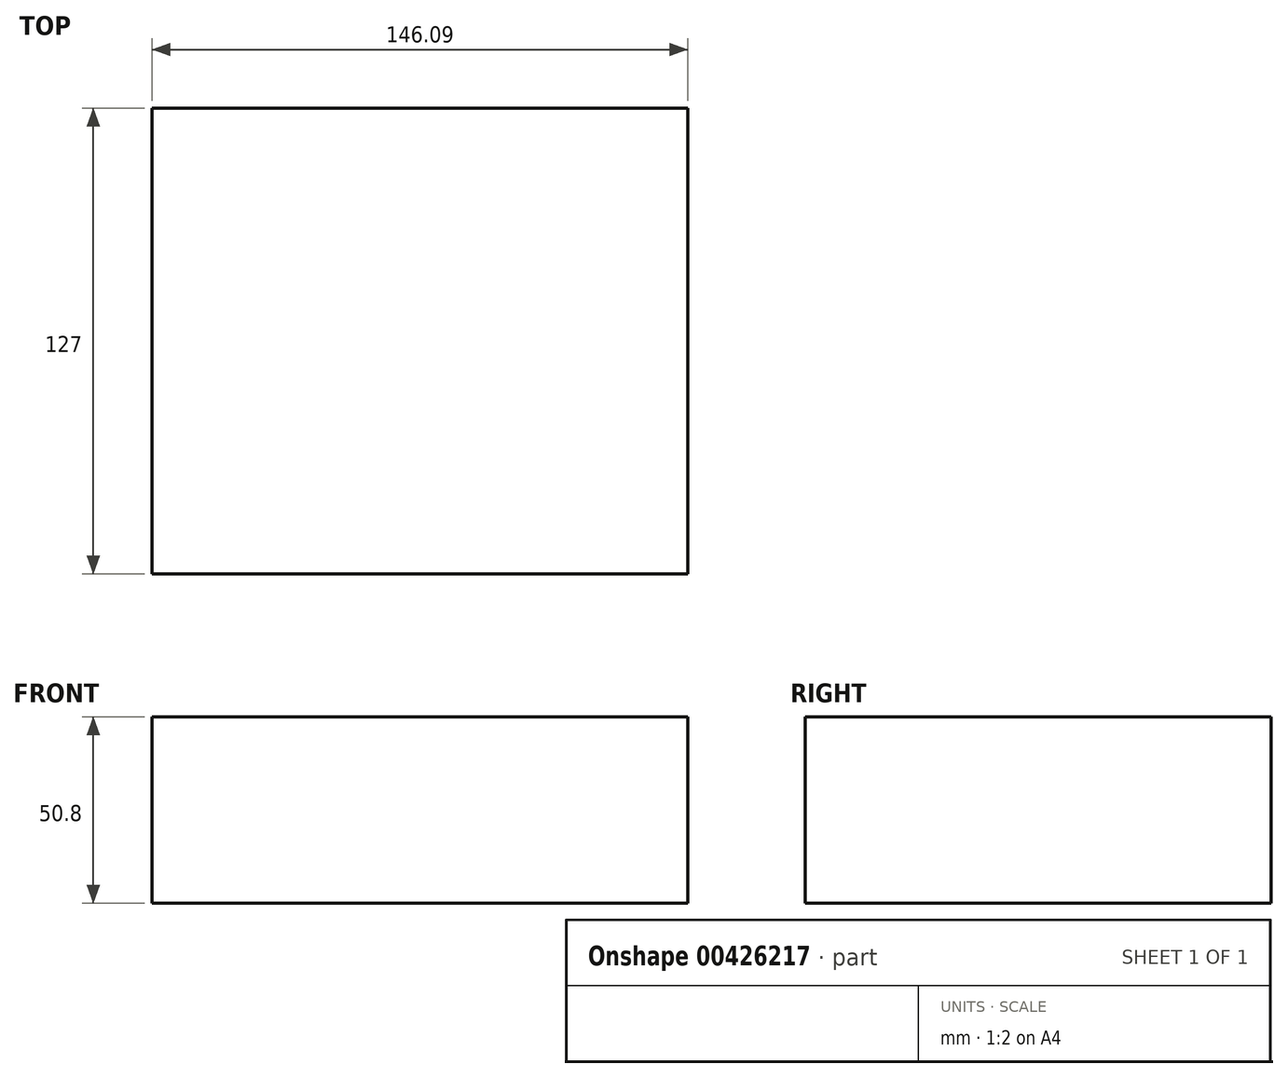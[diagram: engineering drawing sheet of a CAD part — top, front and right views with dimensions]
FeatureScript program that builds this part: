
annotation { "Feature Type Name" : "Feature", "Feature Type Description" : "" }
export const myFeature = defineFeature(function(context is Context, id is Id, definition is map)
    precondition{}
    {
        {
            var Q0;
            Q0=qCreatedBy(makeId("Front.planeOp"),FACE);
            var sketch = newSketch(context, id + "F0", { "sketchPlane" : qUnion([Q0])});
            skLineSegment(sketch, "E0", {"start": v(-6.3, 0) * mm, "end": v(146.1, 0) * mm});
            skLineSegment(sketch, "E1", {"start": v(146.1, 0) * mm, "end": v(146.1, 50.8) * mm});
            skLineSegment(sketch, "E2", {"start": v(146.1, 50.8) * mm, "end": v(0, 50.8) * mm});
            skLineSegment(sketch, "E3", {"start": v(0, 50.8) * mm, "end": v(0, 0) * mm});
            skSolve(sketch);
        }
        {
            var Q0;
            {var subQ0=sQuery(id+"F0.wireOp",EDGE,"E1");Q0=makeQuery(id+"F0.imprint","IMPRINT",FACE,{"disambiguationData":[TD([[makeQuery(id+"F0.imprint","IMPRINT",EDGE,{"derivedFrom":subQ0}),1.0]])]});}
            extrude(context, id + "F1", {"entities" : qUnion([Q0]), "depth" : 76.2 * mm});
        }
        {
            var Q0;
            Q0=makeQuery(id+"F1.opExtrude","CAP_FACE",FACE,{"disambiguationData":[OSD([sQuery(id+"F0.wireOp",EDGE,"E0"),sQuery(id+"F0.wireOp",EDGE,"E1"),sQuery(id+"F0.wireOp",EDGE,"E2"),sQuery(id+"F0.wireOp",EDGE,"E3")])],"isStart":false});
            extrude(context, id + "F2", {"entities" : qUnion([Q0]), "operationType" : NewBodyOperationType.ADD, "depth" : 50.8 * mm});
        }
    });
